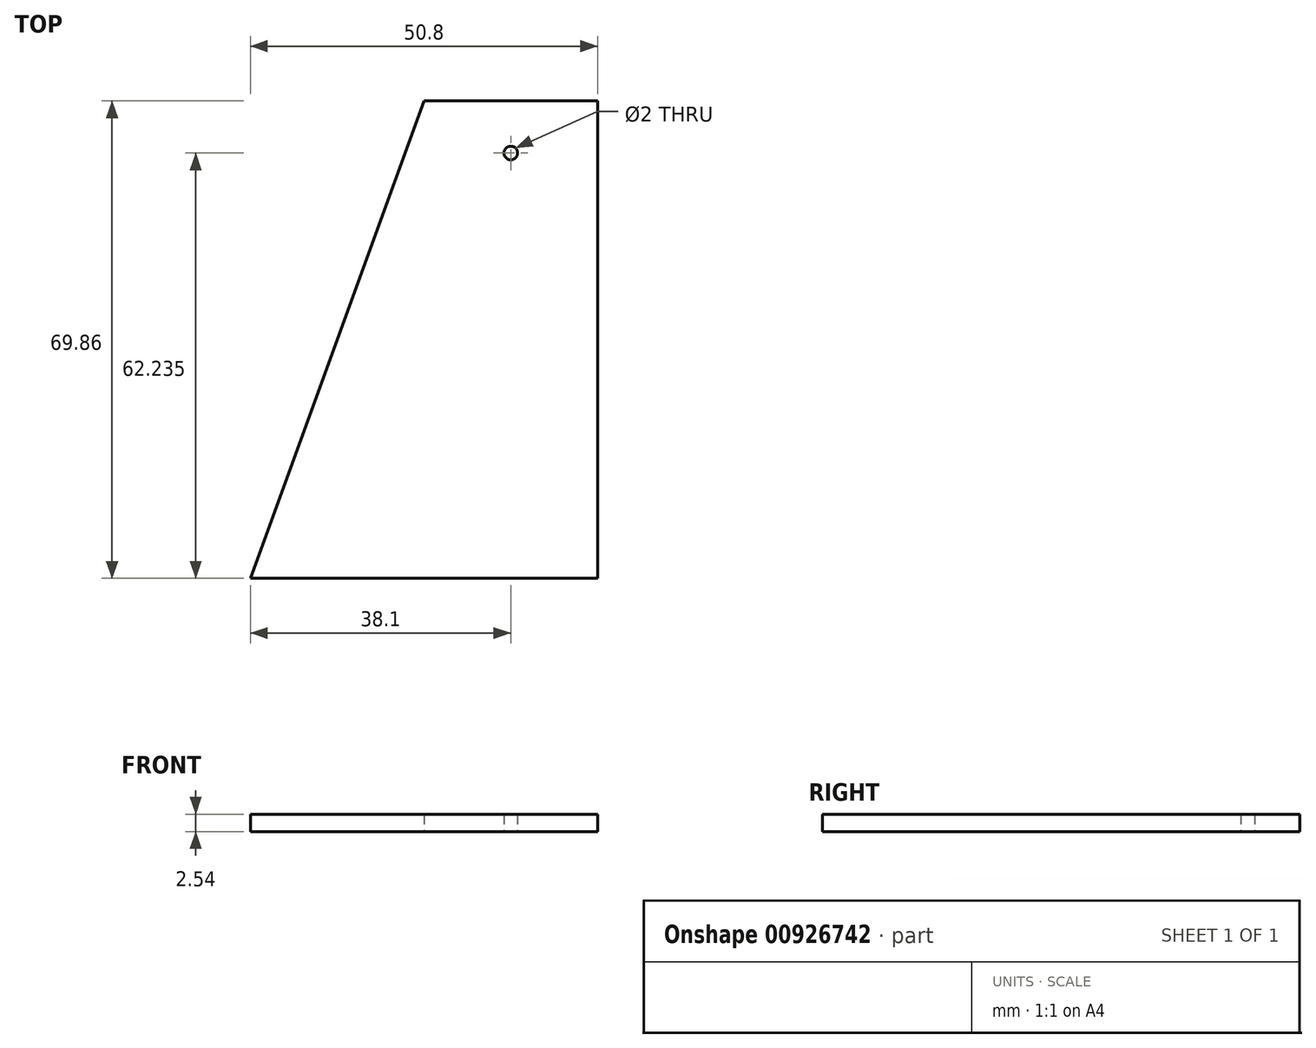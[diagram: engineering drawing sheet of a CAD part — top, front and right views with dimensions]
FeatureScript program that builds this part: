
annotation { "Feature Type Name" : "Feature", "Feature Type Description" : "" }
export const myFeature = defineFeature(function(context is Context, id is Id, definition is map)
    precondition{}
    {
        {
            var Q0;
            Q0=qCreatedBy(makeId("Top.planeOp"),FACE);
            var sketch = newSketch(context, id + "F0", { "sketchPlane" : qUnion([Q0])});
            skLineSegment(sketch, "E0.bottom", {"start": v(25.4, 34.93) * mm, "end": v(0, 34.93) * mm});
            skLineSegment(sketch, "E0.top", {"start": v(25.4, -34.93) * mm, "end": v(-25.4, -34.93) * mm});
            skLineSegment(sketch, "E0.left", {"start": v(25.4, 34.93) * mm, "end": v(25.4, -34.93) * mm});
            skPoint(sketch, "E0.middle", {"position": v(0, 0) * mm});
            skLineSegment(sketch, "E1", {"start": v(0, 34.93) * mm, "end": v(-25.4, -34.93) * mm});
            skPoint(sketch, "E0.right.start.orphan", {"position": v(-25.4, 34.93) * mm});
            skLineSegment(sketch, "E2", {"start": v(0, 34.93) * mm, "end": v(12.7, 34.93) * mm});
            skLineSegment(sketch, "E3", {"start": v(12.7, 34.93) * mm, "end": v(12.7, 27.3) * mm});
            skCircle(sketch, "E4", {"center": v(12.7, 27.3) * mm, "radius": 1 * mm});
            skSolve(sketch);
        }
        {
            var Q0;
            Q0=makeQuery(id+"F0.imprint","IMPRINT",FACE,{"disambiguationData":[TD([[makeQuery(id+"F0.imprint","IMPRINT",EDGE,{"derivedFrom":sQuery(id+"F0.wireOp",EDGE,"E0.bottom")}),1.0]])]});
            extrude(context, id + "F1", {"entities" : qUnion([Q0]), "endBound" : BoundingType.SYMMETRIC, "depth" : 2.54 * mm, "offsetDistance" : 25.4 * mm});
        }
    });
